# Revit family: Kiwi Wall
name_source: partatom
category: Lighting Fixtures
revit_build: Autodesk Revit 2018 (Build: 20170927_1515(x64)
units: mm (PartAtom-declared; Revit-internal decimal feet)

## family parameters
Always vertical = Yes
Cut with Voids When Loaded = No
Host = Wall
Light Source = Yes
OmniClass Number = 23.80.70.00
OmniClass Title = Lighting
Part Type = Normal
Room Calculation Point = No
Round Connector Dimension = Use Diameter
Shared = No

## types (2) — shared parameters
Color Filter = 16777215
Dimming Lamp Color Temperature Shift = <None>
Driver Required = No
Manufacturer = Astro Lighting Ltd
Product Location = Bathroom
URL = www.astrolighting.com

## per-type parameters (varying)
| type | ADA compliant | Apparent Load | Dimmable | Dimming Method | Driver Included | Efficacy (lm/w) | Electrical Class | Lamp | Length of Cable Supplied | Light Source Fixed | Location rating | Main Finish | Main Material | Photometric Web File | Power (Watts) | Product Code | Product Name | Product SKU | Tilt Angle | Wattage Comments |
| CE | Not Applicable | 9 VA | No | Not Applicable | Yes (Integral) | 78.81 | 2 | LED | Not Applicable | Yes | IP44 | Various | Metal - Zinc | GNC-19595  8010 - Kiwi Wall ies.ies | 7.2 | 8008 | Kiwi Wall | 1390001 | 90.00° | Not Applicable |
| ETL | NO | 0 VA |  |  |  |  | 0 |  |  |  | DAMP |  | Metal - Steel | generic |  | 1234 |  | 1234001 | 60.00° |  |

## geometry (parser evidence)
native form markers: Sweep x1
no freeform markers — native parametric forms only
